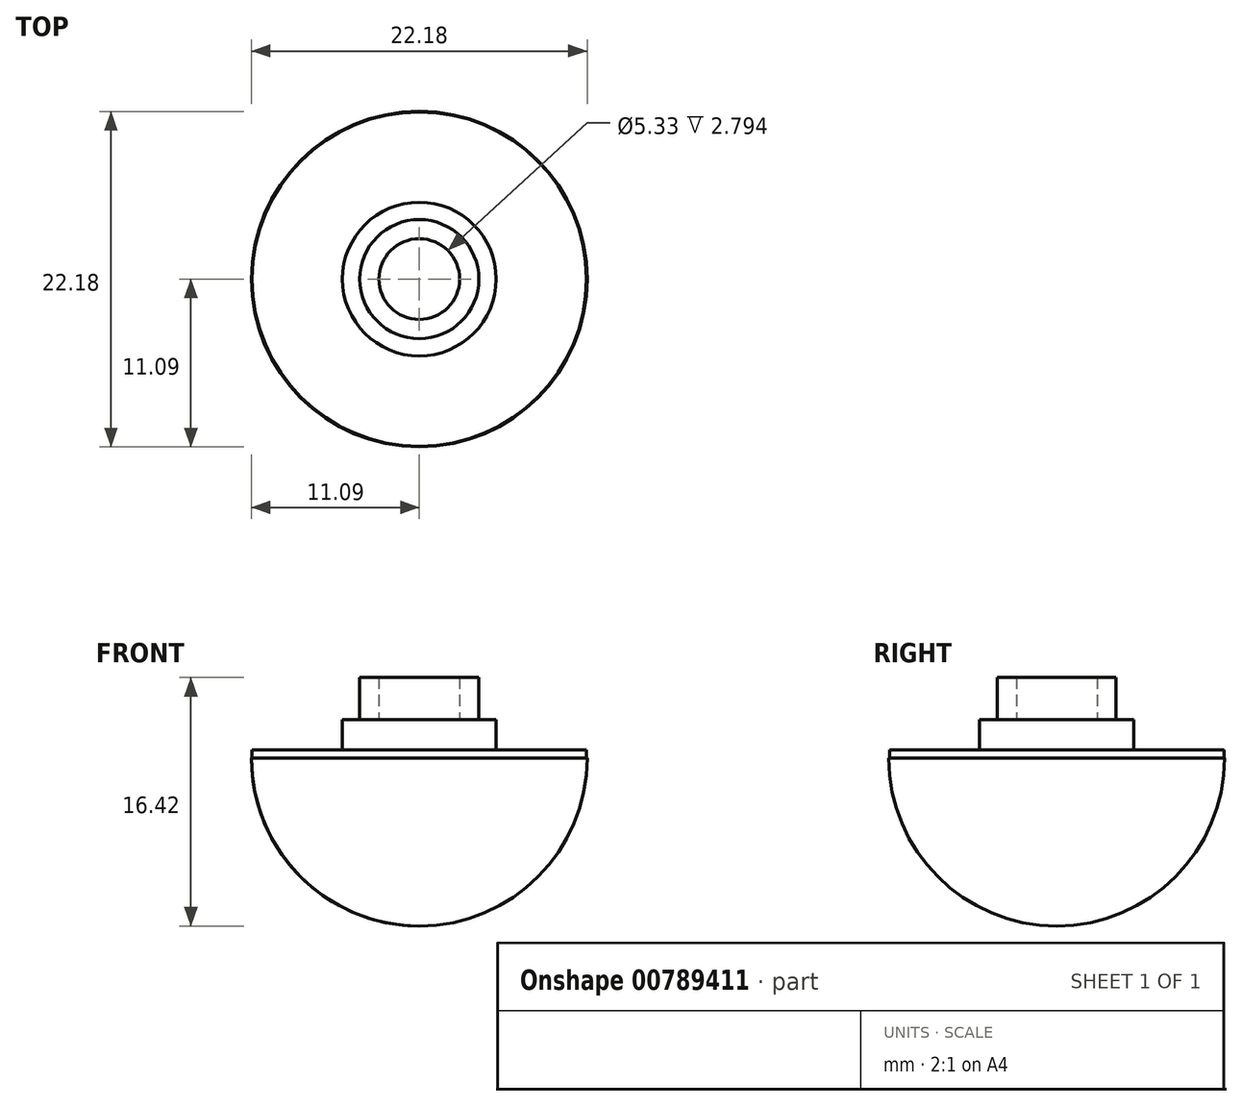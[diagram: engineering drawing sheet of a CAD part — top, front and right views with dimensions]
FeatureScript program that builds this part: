
annotation { "Feature Type Name" : "Feature", "Feature Type Description" : "" }
export const myFeature = defineFeature(function(context is Context, id is Id, definition is map)
    precondition{}
    {
        {
            var Q0;
            Q0=qCreatedBy(makeId("Top.planeOp"),FACE);
            var sketch = newSketch(context, id + "F0", { "sketchPlane" : qUnion([Q0])});
            skCircle(sketch, "E0", {"center": v(0, 0) * mm, "radius": 3.94 * mm});
            skCircle(sketch, "E1.0", {"center": v(0, 0) * mm, "radius": 2.67 * mm});
            skSolve(sketch);
        }
        {
            var Q0;
            Q0=qSketchRegion(id+"F0",true);
            extrude(context, id + "F1", {"entities" : qUnion([Q0]), "depth" : 2.8 * mm, "offsetDistance" : 25.4 * mm});
        }
        {
            var Q0;
            Q0=makeQuery(id+"F1.opExtrude","CAP_FACE",FACE,{"disambiguationData":[OSD([sQuery(id+"F0.wireOp",EDGE,"E0"),sQuery(id+"F0.wireOp",EDGE,"E1.0")])],"isStart":true});
            var sketch = newSketch(context, id + "F2", { "sketchPlane" : qUnion([Q0])});
            skCircle(sketch, "E2", {"center": v(0, 0) * mm, "radius": 5.08 * mm});
            skSolve(sketch);
        }
        {
            var Q0;
            Q0=qSketchRegion(id+"F2",true);
            extrude(context, id + "F3", {"entities" : qUnion([Q0]), "operationType" : NewBodyOperationType.ADD, "depth" : 1.98 * mm, "offsetDistance" : 25.4 * mm});
        }
        {
            var Q0;
            Q0=makeQuery(id+"F3.opExtrude","CAP_FACE",FACE,{"disambiguationData":[OSD([sQuery(id+"F2.wireOp",EDGE,"E2")])],"isStart":false});
            var sketch = newSketch(context, id + "F4", { "sketchPlane" : qUnion([Q0])});
            skCircle(sketch, "E3", {"center": v(0, 0) * mm, "radius": 11.05 * mm});
            skSolve(sketch);
        }
        {
            var Q0;
            Q0=qSketchRegion(id+"F4",true);
            extrude(context, id + "F5", {"entities" : qUnion([Q0]), "operationType" : NewBodyOperationType.ADD, "depth" : 1.52 * mm, "offsetDistance" : 25.4 * mm});
        }
        {
            var Q0;
            Q0=qCreatedBy(makeId("Front.planeOp"),FACE);
            var sketch = newSketch(context, id + "F6", { "sketchPlane" : qUnion([Q0])});
            skCircle(sketch, "E4", {"center": v(0, -2.54) * mm, "radius": 11.1 * mm});
            skLineSegment(sketch, "E5", {"start": v(0, -3.56) * mm, "end": v(0, -13.63) * mm});
            skLineSegment(sketch, "E6", {"start": v(0, -2.54) * mm, "end": v(-11.1, -2.54) * mm});
            skLineSegment(sketch, "E7", {"start": v(0, -3.56) * mm, "end": v(0, -2.54) * mm});
            skSolve(sketch);
        }
        {
            var Q0;
            {var subQ0=sQuery(id+"F6.wireOp",EDGE,"EOfANily-kuZe-bkNX-dxyu-0azTl8kxperc");Q0=makeQuery(id+"F6.imprint","IMPRINT",FACE,{"disambiguationData":[TD([[makeQuery(id+"F6.imprint","IMPRINT",EDGE,{"derivedFrom":subQ0}),1.0]])]});}
            var Q1;
            {var subQ0=sQuery(id+"F6.wireOp",EDGE,"E5");Q1=makeQuery(id+"F6.imprint","IMPRINT",FACE,{"disambiguationData":[TD([[makeQuery(id+"F6.imprint","IMPRINT",EDGE,{"derivedFrom":subQ0}),-1.0]])]});}
            var Q2;
            Q2=sQuery(id+"F6.wireOp",EDGE,"E5");
            revolve(context, id + "F7", {"operationType" : NewBodyOperationType.ADD, "surfaceOperationType" : NewSurfaceOperationType.NEW, "entities" : qUnion([Q0, Q1]), "axis" : qUnion([Q2]), "revolveType" : RevolveType.FULL});
        }
    });
